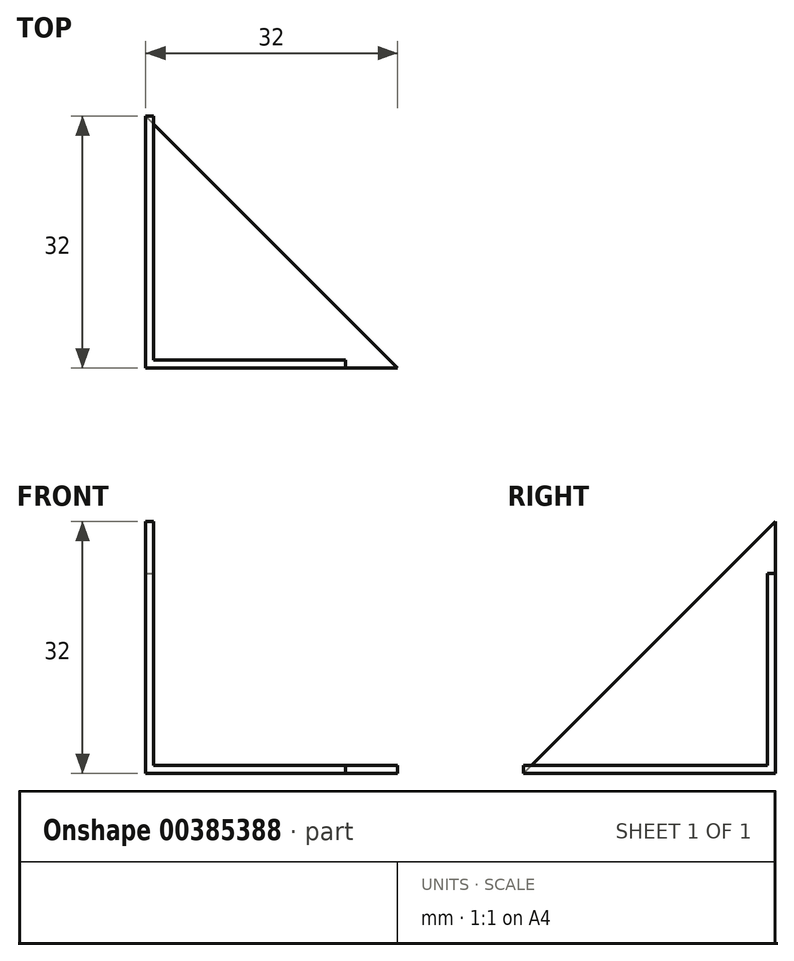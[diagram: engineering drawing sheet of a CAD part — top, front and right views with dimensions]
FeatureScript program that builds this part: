
annotation { "Feature Type Name" : "Feature", "Feature Type Description" : "" }
export const myFeature = defineFeature(function(context is Context, id is Id, definition is map)
    precondition{}
    {
        {
            var Q0;
            Q0=qCreatedBy(makeId("Front.planeOp"),FACE);
            var sketch = newSketch(context, id + "F0", { "sketchPlane" : qUnion([Q0])});
            skLineSegment(sketch, "E0", {"start": v(-11, 21) * mm, "end": v(-11, -11) * mm});
            skLineSegment(sketch, "E1", {"start": v(-11, -11) * mm, "end": v(21, -11) * mm});
            skLineSegment(sketch, "E2", {"start": v(21, -11) * mm, "end": v(21, -10) * mm});
            skLineSegment(sketch, "E3", {"start": v(21, -10) * mm, "end": v(-10, -10) * mm});
            skLineSegment(sketch, "E4", {"start": v(-10, -10) * mm, "end": v(-10, 21) * mm});
            skLineSegment(sketch, "E5", {"start": v(-10, 21) * mm, "end": v(-11, 21) * mm});
            skSolve(sketch);
        }
        {
            var Q0;
            Q0 = qSketchRegion(id + "F0", true);
            extrude(context, id + "F1", {"entities" : qUnion([Q0]), "depth" : 32 * mm});
        }
        {
            var Q0;
            Q0=makeQuery(id+"F1.opExtrude","SWEPT_FACE",FACE,{"disambiguationData":[OSD([sQuery(id+"F0.wireOp",EDGE,"E0")])]});
            var sketch = newSketch(context, id + "F2", { "sketchPlane" : qUnion([Q0])});
            skLineSegment(sketch, "E6", {"start": v(0, -11) * mm, "end": v(32, 21) * mm});
            skLineSegment(sketch, "E7", {"start": v(32, 21) * mm, "end": v(0, 21) * mm});
            skLineSegment(sketch, "E8", {"start": v(0, 21) * mm, "end": v(32, -11) * mm});
            skPoint(sketch, "E9", {"position": v(16, 5) * mm});
            skCircle(sketch, "E10", {"center": v(16, 5) * mm, "radius": 2.54 * mm});
            skSolve(sketch);
        }
        {
            var Q0;
            {var subQ0=sQuery(id+"F2.wireOp",EDGE,"E10");var subQ1=sQuery(id+"F2.wireOp",EDGE,"E6");var subQ2=makeQuery(id+"F2.imprint","INTERSECT",VERTEX,{"disambiguationData":[OD(0.0)],"derivedFrom":[subQ1,subQ0]});Q0=makeQuery(id+"F2.imprint","IMPRINT",FACE,{"disambiguationData":[TD([[makeQuery(id+"F2.imprint","IMPRINT",EDGE,{"disambiguationData":[TD([[subQ2,-1.0]])],"derivedFrom":subQ1}),-1.0]])]});}
            var Q1;
            {var subQ0=sQuery(id+"F2.wireOp",EDGE,"E10");var subQ1=sQuery(id+"F2.wireOp",EDGE,"E6");var subQ2=makeQuery(id+"F2.imprint","INTERSECT",VERTEX,{"disambiguationData":[OD(0.0)],"derivedFrom":[subQ1,subQ0]});Q1=makeQuery(id+"F2.imprint","IMPRINT",FACE,{"disambiguationData":[TD([[makeQuery(id+"F2.imprint","IMPRINT",EDGE,{"disambiguationData":[TD([[subQ2,-1.0]])],"derivedFrom":subQ1}),1.0]])]});}
            var Q2;
            {var subQ0=sQuery(id+"F2.wireOp",EDGE,"E8");var subQ1=sQuery(id+"F2.wireOp",EDGE,"E6");var subQ2=makeQuery(id+"F2.imprint","INTERSECT",VERTEX,{"derivedFrom":[subQ1,subQ0]});Q2=makeQuery(id+"F2.imprint","IMPRINT",FACE,{"disambiguationData":[TD([[makeQuery(id+"F2.imprint","IMPRINT",EDGE,{"disambiguationData":[TD([[subQ2,-1.0]])],"derivedFrom":subQ1}),1.0]])]});}
            var Q3;
            {var subQ0=sQuery(id+"F2.wireOp",EDGE,"E8");var subQ1=sQuery(id+"F2.wireOp",EDGE,"E6");var subQ2=makeQuery(id+"F2.imprint","INTERSECT",VERTEX,{"derivedFrom":[subQ1,subQ0]});Q3=makeQuery(id+"F2.imprint","IMPRINT",FACE,{"disambiguationData":[TD([[makeQuery(id+"F2.imprint","IMPRINT",EDGE,{"disambiguationData":[TD([[subQ2,-1.0]])],"derivedFrom":subQ1}),-1.0]])]});}
            extrude(context, id + "F3", {"entities" : qUnion([Q0, Q1, Q2, Q3]), "operationType" : NewBodyOperationType.REMOVE, "oppositeDirection" : true, "depth" : 25.4 * mm});
        }
        {
            var Q0;
            Q0=makeQuery(id+"F1.opExtrude","SWEPT_FACE",FACE,{"disambiguationData":[OSD([sQuery(id+"F0.wireOp",EDGE,"E1")])]});
            var sketch = newSketch(context, id + "F4", { "sketchPlane" : qUnion([Q0])});
            skLineSegment(sketch, "E11", {"start": v(-11, 32) * mm, "end": v(21, 0) * mm});
            skLineSegment(sketch, "E12", {"start": v(21, 0) * mm, "end": v(21, 32) * mm});
            skLineSegment(sketch, "E13", {"start": v(21, 32) * mm, "end": v(-11, 0) * mm});
            skPoint(sketch, "E14", {"position": v(5, 16) * mm});
            skCircle(sketch, "E15", {"center": v(5, 16) * mm, "radius": 2.54 * mm});
            skSolve(sketch);
        }
        {
            var Q0;
            {var subQ0=sQuery(id+"F4.wireOp",EDGE,"E13");var subQ1=sQuery(id+"F4.wireOp",EDGE,"E11");var subQ2=makeQuery(id+"F4.imprint","INTERSECT",VERTEX,{"derivedFrom":[subQ1,subQ0]});Q0=makeQuery(id+"F4.imprint","IMPRINT",FACE,{"disambiguationData":[TD([[makeQuery(id+"F4.imprint","IMPRINT",EDGE,{"disambiguationData":[TD([[subQ2,-1.0]])],"derivedFrom":subQ1}),1.0]])]});}
            var Q1;
            {var subQ0=sQuery(id+"F4.wireOp",EDGE,"E15");var subQ1=sQuery(id+"F4.wireOp",EDGE,"E11");var subQ2=makeQuery(id+"F4.imprint","INTERSECT",VERTEX,{"disambiguationData":[OD(0.0)],"derivedFrom":[subQ1,subQ0]});Q1=makeQuery(id+"F4.imprint","IMPRINT",FACE,{"disambiguationData":[TD([[makeQuery(id+"F4.imprint","IMPRINT",EDGE,{"disambiguationData":[TD([[subQ2,-1.0]])],"derivedFrom":subQ1}),1.0]])]});}
            var Q2;
            {var subQ0=sQuery(id+"F4.wireOp",EDGE,"E13");var subQ1=sQuery(id+"F4.wireOp",EDGE,"E11");var subQ2=makeQuery(id+"F4.imprint","INTERSECT",VERTEX,{"derivedFrom":[subQ1,subQ0]});Q2=makeQuery(id+"F4.imprint","IMPRINT",FACE,{"disambiguationData":[TD([[makeQuery(id+"F4.imprint","IMPRINT",EDGE,{"disambiguationData":[TD([[subQ2,-1.0]])],"derivedFrom":subQ1}),-1.0]])]});}
            var Q3;
            {var subQ0=sQuery(id+"F4.wireOp",EDGE,"E15");var subQ1=sQuery(id+"F4.wireOp",EDGE,"E11");var subQ2=makeQuery(id+"F4.imprint","INTERSECT",VERTEX,{"disambiguationData":[OD(0.0)],"derivedFrom":[subQ1,subQ0]});Q3=makeQuery(id+"F4.imprint","IMPRINT",FACE,{"disambiguationData":[TD([[makeQuery(id+"F4.imprint","IMPRINT",EDGE,{"disambiguationData":[TD([[subQ2,-1.0]])],"derivedFrom":subQ1}),-1.0]])]});}
            extrude(context, id + "F5", {"entities" : qUnion([Q0, Q1, Q2, Q3]), "operationType" : NewBodyOperationType.REMOVE, "oppositeDirection" : true, "depth" : 25.4 * mm});
        }
    });
